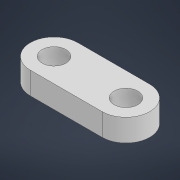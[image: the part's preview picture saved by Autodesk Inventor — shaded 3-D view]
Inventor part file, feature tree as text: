
AUTODESK INVENTOR PART (.ipt)
format: ipt  version: 2021 (Build 250183000, 183)  size: 107,008 bytes
history: native  units: mm
features: sketch x2, extrude x1, hole x1
ambient origin geometry x8: Origin, YZ Plane, XZ Plane, XY Plane, X Axis, Y Axis, Z Axis, Center Point
bodies: Solid1 (feature_tree)
feature tree (4):
  extrude  "Extrusion1"  Depth=8.0mm
  hole  "Hole1"  [1 undecoded]
  sketch  "Sketch1"  dims[d0=16.0mm d2=8.0mm]
  sketch  "Sketch2"  dims[d4=24.226mm d5=12.113mm d6=7.5mm d7=0.0mm d8=0.0mm d9=0.0mm d11=0.0mm d12=0.0mm d13=8.0mm d14=6.0mm d15=4.0mm d16=2.0mm d17=90.0deg d18=8.0mm d19=20.594885mm]
note: 1 required parameter value undecoded (feature->parameter linkage not recoverable at this tier; creation-order binding heuristic only, values carry confidence <= 0.55)
